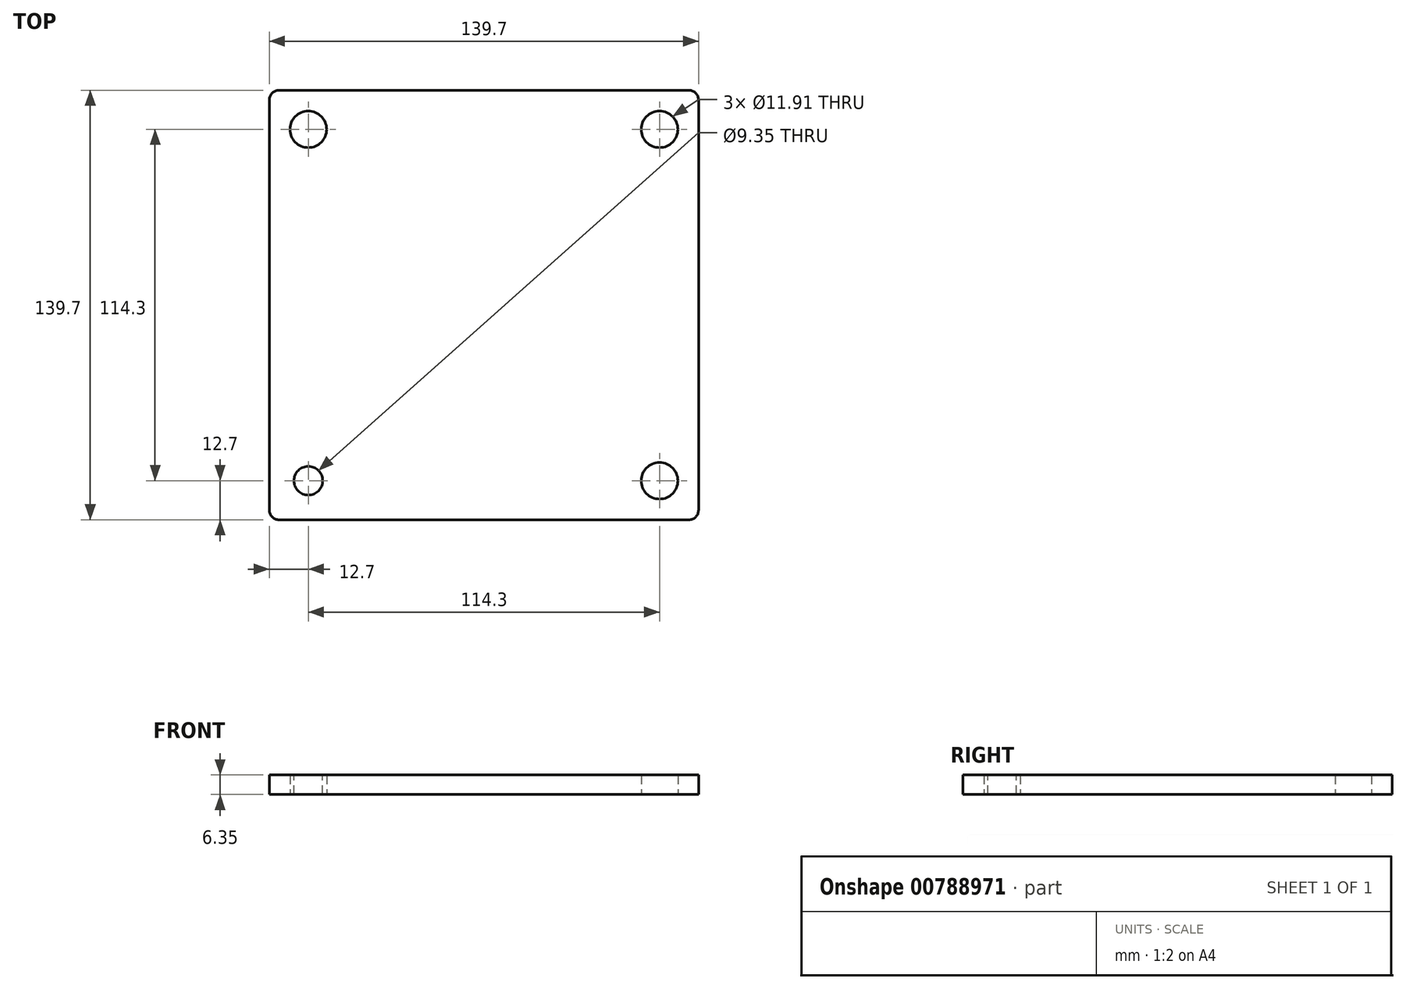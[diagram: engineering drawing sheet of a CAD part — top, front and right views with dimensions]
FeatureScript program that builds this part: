
annotation { "Feature Type Name" : "Feature", "Feature Type Description" : "" }
export const myFeature = defineFeature(function(context is Context, id is Id, definition is map)
    precondition{}
    {
        {
            var Q0;
            Q0=qCreatedBy(makeId("Top.planeOp"),FACE);
            var sketch = newSketch(context, id + "F0", { "sketchPlane" : qUnion([Q0])});
            skLineSegment(sketch, "E0.bottom", {"start": v(-69.85, 69.85) * mm, "end": v(69.85, 69.85) * mm});
            skLineSegment(sketch, "E0.top", {"start": v(-69.85, -69.85) * mm, "end": v(69.85, -69.85) * mm});
            skLineSegment(sketch, "E0.left", {"start": v(-69.85, 69.85) * mm, "end": v(-69.85, -69.85) * mm});
            skLineSegment(sketch, "E0.right", {"start": v(69.85, 69.85) * mm, "end": v(69.85, -69.85) * mm});
            skCircle(sketch, "E1", {"center": v(57.15, 57.15) * mm, "radius": 5.95 * mm});
            skLineSegment(sketch, "E2.direction1", {"start": v(57.15, 57.15) * mm, "end": v(-57.15, 57.15) * mm, "construction": true});
            skLineSegment(sketch, "E2.direction2", {"start": v(57.15, 57.15) * mm, "end": v(57.15, -57.15) * mm, "construction": true});
            skCircle(sketch, "E3.0.1.0", {"center": v(-57.15, 57.15) * mm, "radius": 5.95 * mm});
            skCircle(sketch, "E4.0.0.1", {"center": v(57.15, -57.15) * mm, "radius": 5.95 * mm});
            skCircle(sketch, "E4.0.1.1", {"center": v(-57.15, -57.15) * mm, "radius": 5.95 * mm});
            skSolve(sketch);
        }
        {
            var Q0;
            Q0 = qSketchRegion(id + "F0", true);
            var Q1;
            Q1=makeQuery(id+"F0.imprint","IMPRINT",FACE,{"disambiguationData":[TD([[makeQuery(id+"F0.imprint","IMPRINT",EDGE,{"derivedFrom":sQuery(id+"F0.wireOp",EDGE,"E4.0.1.1")}),1.0]])]});
            extrude(context, id + "F1", {"entities" : qUnion([Q0, Q1]), "depth" : 6.35 * mm, "offsetDistance" : 25.4 * mm});
        }
        {
            var Q0;
            Q0=makeQuery(id+"F1.opExtrude","CAP_FACE",FACE,{"disambiguationData":[OSD([sQuery(id+"F0.wireOp",EDGE,"E0.bottom"),sQuery(id+"F0.wireOp",EDGE,"E0.top"),sQuery(id+"F0.wireOp",EDGE,"E0.left"),sQuery(id+"F0.wireOp",EDGE,"E0.right"),sQuery(id+"F0.wireOp",EDGE,"E1"),sQuery(id+"F0.wireOp",EDGE,"E2.1.0.0")])],"isStart":false});
            var sketch = newSketch(context, id + "F2", { "sketchPlane" : qUnion([Q0])});
            skPoint(sketch, "E5", {"position": v(-57.15, -57.15) * mm});
            skSolve(sketch);
        }
        {
            var Q0;
            Q0=sQuery(id+"F2.wireOp",VERTEX,"E5");
            var Q1;
            Q1=makeQuery(id+"F1.opExtrude","SWEPT_BODY",BODY,{"disambiguationData":[OSD([sQuery(id+"F0.wireOp",EDGE,"E0.bottom"),sQuery(id+"F0.wireOp",EDGE,"E0.top"),sQuery(id+"F0.wireOp",EDGE,"E0.left"),sQuery(id+"F0.wireOp",EDGE,"E0.right"),sQuery(id+"F0.wireOp",EDGE,"E1"),sQuery(id+"F0.wireOp",EDGE,"E2.1.0.0")])]});
            hole(context, id + "F3", {"style" : HoleStyle.SIMPLE, "endStyle" : HoleEndStyle.THROUGH, "standardTappedOrClearance" : lookupTablePath({ "standard" : "ANSI", "engagement" : "75%", "pitch" : "14 tpi", "size" : "7/16", "type" : "Tapped" }), "standardBlindInLast" : lookupTablePath({ "standard" : "ANSI", "engagement" : "75%", "pitch" : "14 tpi", "size" : "7/16", "type" : "Tapped" }), "holeDiameter" : 9.35 * mm, "majorDiameter" : 11.1 * mm, "showTappedDepth" : true, "isTappedThrough" : true, "tappedDepth" : 12.7 * mm, "tapClearance" : 3, "locations" : qUnion([Q0]), "scope" : qUnion([Q1])});
        }
        {
            var Q0;
            Q0=makeQuery(id+"F1.opExtrude","SWEPT_EDGE",EDGE,{"disambiguationData":[OSD([sQuery(id+"F0.wireOp",EDGE,"E0.bottom"),sQuery(id+"F0.wireOp",EDGE,"E0.left")])]});
            fillet(context, id + "F4", {"entities" : qUnion([Q0]), "radius" : 3.17 * mm, "tangentPropagation" : true, "allowEdgeOverflow" : false});
        }
        {
            var Q0;
            Q0=makeQuery(id+"F1.opExtrude","SWEPT_EDGE",EDGE,{"disambiguationData":[OSD([sQuery(id+"F0.wireOp",EDGE,"E0.bottom"),sQuery(id+"F0.wireOp",EDGE,"E0.right")])]});
            fillet(context, id + "F5", {"entities" : qUnion([Q0]), "radius" : 3.17 * mm, "tangentPropagation" : true, "allowEdgeOverflow" : false});
        }
        {
            var Q0;
            Q0=makeQuery(id+"F1.opExtrude","SWEPT_EDGE",EDGE,{"disambiguationData":[OSD([sQuery(id+"F0.wireOp",EDGE,"E0.top"),sQuery(id+"F0.wireOp",EDGE,"E0.right")])]});
            fillet(context, id + "F6", {"entities" : qUnion([Q0]), "radius" : 3.17 * mm, "tangentPropagation" : true, "allowEdgeOverflow" : false});
        }
        {
            var Q0;
            Q0=makeQuery(id+"F1.opExtrude","SWEPT_EDGE",EDGE,{"disambiguationData":[OSD([sQuery(id+"F0.wireOp",EDGE,"E0.top"),sQuery(id+"F0.wireOp",EDGE,"E0.left")])]});
            fillet(context, id + "F7", {"entities" : qUnion([Q0]), "radius" : 3.17 * mm, "tangentPropagation" : true, "allowEdgeOverflow" : false});
        }
    });
